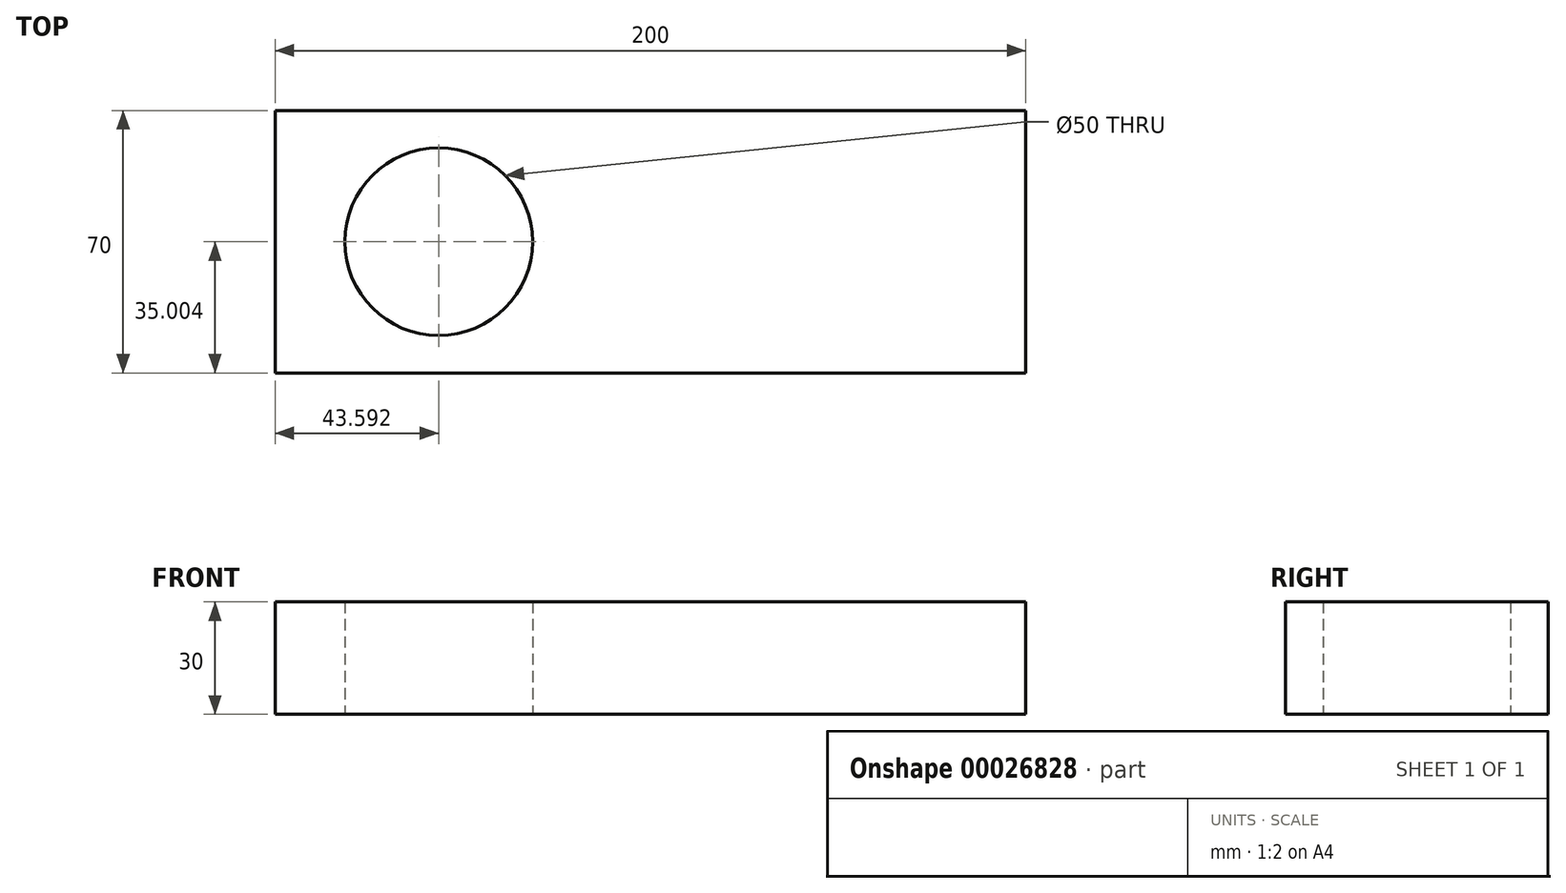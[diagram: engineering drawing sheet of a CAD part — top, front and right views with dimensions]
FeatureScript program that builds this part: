
annotation { "Feature Type Name" : "Feature", "Feature Type Description" : "" }
export const myFeature = defineFeature(function(context is Context, id is Id, definition is map)
    precondition{}
    {
        {
            var Q0;
            Q0=qCreatedBy(makeId("Top.planeOp"),FACE);
            var sketch = newSketch(context, id + "F0", { "sketchPlane" : qUnion([Q0])});
            skLineSegment(sketch, "E0.bottom", {"start": v(-105.9, 13.81) * mm, "end": v(94.1, 13.81) * mm});
            skLineSegment(sketch, "E0.top", {"start": v(-105.9, -56.19) * mm, "end": v(94.1, -56.19) * mm});
            skLineSegment(sketch, "E0.left", {"start": v(-105.9, 13.81) * mm, "end": v(-105.9, -56.19) * mm});
            skLineSegment(sketch, "E0.right", {"start": v(94.1, 13.81) * mm, "end": v(94.1, -56.19) * mm});
            skLineSegment(sketch, "E1", {"start": v(-105.9, -21.19) * mm, "end": v(-105.9, -56.19) * mm});
            skLineSegment(sketch, "E2", {"start": v(-105.9, -21.19) * mm, "end": v(94.1, -21.19) * mm});
            skCircle(sketch, "E3", {"center": v(-62.32, -21.19) * mm, "radius": 25 * mm});
            skSolve(sketch);
        }
        {
            var Q0;
            {var subQ7=sQuery(id+"F0.wireOp",EDGE,"E0.bottom");Q0=makeQuery(id+"F0.imprint","IMPRINT",FACE,{"disambiguationData":[TD([[makeQuery(id+"F0.imprint","IMPRINT",EDGE,{"derivedFrom":subQ7}),-1.0]])]});}
            var Q1;
            {var subQ7=sQuery(id+"F0.wireOp",EDGE,"E0.top");Q1=makeQuery(id+"F0.imprint","IMPRINT",FACE,{"disambiguationData":[TD([[makeQuery(id+"F0.imprint","IMPRINT",EDGE,{"derivedFrom":subQ7}),1.0]])]});}
            extrude(context, id + "F1", {"entities" : qUnion([Q0, Q1]), "depth" : 30 * mm});
        }
    });
